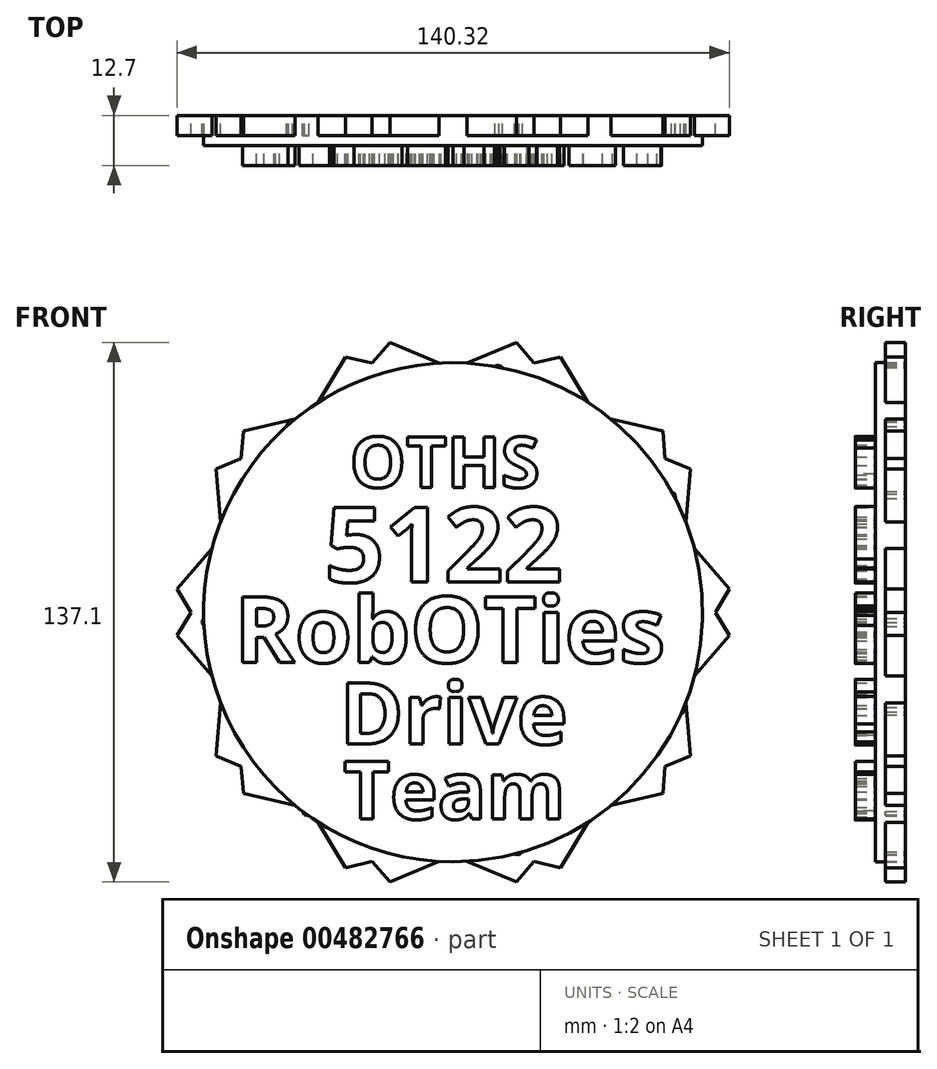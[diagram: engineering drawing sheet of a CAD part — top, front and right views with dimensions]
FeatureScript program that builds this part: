
annotation { "Feature Type Name" : "Feature", "Feature Type Description" : "" }
export const myFeature = defineFeature(function(context is Context, id is Id, definition is map)
    precondition{}
    {
        {
            var Q0;
            Q0=qCreatedBy(makeId("Front.planeOp"),FACE);
            var sketch = newSketch(context, id + "F0", { "sketchPlane" : qUnion([Q0])});
            skCircle(sketch, "E0.cCircle", {"center": v(0, 0) * mm, "radius": 63.4 * mm, "construction": true});
            skLineSegment(sketch, "E0.0", {"start": v(49.97, -39.02) * mm, "end": v(-8.8, -62.79) * mm});
            skLineSegment(sketch, "E0.1", {"start": v(-8.8, -62.79) * mm, "end": v(-58.78, -23.77) * mm});
            skLineSegment(sketch, "E0.2", {"start": v(-58.78, -23.77) * mm, "end": v(-49.97, 39.02) * mm});
            skLineSegment(sketch, "E0.3", {"start": v(-49.97, 39.02) * mm, "end": v(8.8, 62.79) * mm});
            skLineSegment(sketch, "E0.4", {"start": v(8.8, 62.79) * mm, "end": v(58.78, 23.77) * mm});
            skLineSegment(sketch, "E0.5", {"start": v(58.78, 23.77) * mm, "end": v(49.97, -39.02) * mm});
            skCircle(sketch, "E1", {"center": v(0, 0) * mm, "radius": 63.4 * mm});
            skSolve(sketch);
        }
        {
            var Q0;
            Q0=qSketchRegion(id+"F0",true);
            extrude(context, id + "F1", {"entities" : qUnion([Q0]), "depth" : 7.62 * mm});
        }
        {
            var Q0;
            Q0=qCreatedBy(makeId("Front.planeOp"),FACE);
            var sketch = newSketch(context, id + "F2", { "sketchPlane" : qUnion([Q0])});
            skCircle(sketch, "E2.cCircle", {"center": v(0, 0) * mm, "radius": 56.96 * mm, "construction": true});
            skLineSegment(sketch, "E2.0", {"start": v(70.16, -5.91) * mm, "end": v(16.06, -68.55) * mm});
            skLineSegment(sketch, "E2.1", {"start": v(16.06, -68.55) * mm, "end": v(-60.23, -36.45) * mm});
            skLineSegment(sketch, "E2.2", {"start": v(-60.23, -36.45) * mm, "end": v(-53.28, 46.02) * mm});
            skLineSegment(sketch, "E2.3", {"start": v(-53.28, 46.02) * mm, "end": v(27.3, 64.9) * mm});
            skLineSegment(sketch, "E2.4", {"start": v(27.3, 64.9) * mm, "end": v(70.16, -5.91) * mm});
            skPoint(sketch, "E2.0.midPoint", {"position": v(43.1, -37.23) * mm});
            skLineSegment(sketch, "E3.MirrorCS", {"start": v(-53.28, -46.02) * mm, "end": v(27.3, -64.9) * mm});
            skLineSegment(sketch, "E4.MirrorCS", {"start": v(27.3, -64.9) * mm, "end": v(70.16, 5.91) * mm});
            skLineSegment(sketch, "E5.MirrorCS", {"start": v(-60.23, 36.45) * mm, "end": v(-53.28, -46.02) * mm});
            skLineSegment(sketch, "E6.MirrorCS", {"start": v(70.16, 5.91) * mm, "end": v(16.06, 68.55) * mm});
            skLineSegment(sketch, "E7.MirrorCS", {"start": v(16.06, 68.55) * mm, "end": v(-60.23, 36.45) * mm});
            skLineSegment(sketch, "E8.MirrorCS", {"start": v(-27.3, 64.9) * mm, "end": v(-70.16, -5.91) * mm});
            skLineSegment(sketch, "E9.MirrorCS", {"start": v(-70.16, 5.91) * mm, "end": v(-16.06, 68.55) * mm});
            skLineSegment(sketch, "E10.MirrorCS", {"start": v(53.28, 46.02) * mm, "end": v(-27.3, 64.9) * mm});
            skLineSegment(sketch, "E11.MirrorCS", {"start": v(-16.06, 68.55) * mm, "end": v(60.23, 36.45) * mm});
            skLineSegment(sketch, "E12.MirrorCS", {"start": v(60.23, -36.45) * mm, "end": v(53.28, 46.02) * mm});
            skLineSegment(sketch, "E13.MirrorCS", {"start": v(60.23, 36.45) * mm, "end": v(53.28, -46.02) * mm});
            skLineSegment(sketch, "E14.MirrorCS", {"start": v(-16.06, -68.55) * mm, "end": v(60.23, -36.45) * mm});
            skLineSegment(sketch, "E15.MirrorCS", {"start": v(53.28, -46.02) * mm, "end": v(-27.3, -64.9) * mm});
            skLineSegment(sketch, "E16.MirrorCS", {"start": v(-70.16, -5.91) * mm, "end": v(-16.06, -68.55) * mm});
            skLineSegment(sketch, "E17.MirrorCS", {"start": v(-27.3, -64.9) * mm, "end": v(-70.16, 5.91) * mm});
            skCircle(sketch, "E18.cCircle", {"center": v(0, 0) * mm, "radius": 57.56 * mm, "construction": true});
            skLineSegment(sketch, "E18.0", {"start": v(58.64, -25.36) * mm, "end": v(16.73, -61.66) * mm});
            skLineSegment(sketch, "E18.1", {"start": v(16.73, -61.66) * mm, "end": v(-37.77, -51.52) * mm});
            skLineSegment(sketch, "E18.2", {"start": v(-37.77, -51.52) * mm, "end": v(-63.83, -2.6) * mm});
            skLineSegment(sketch, "E18.3", {"start": v(-63.83, -2.6) * mm, "end": v(-41.83, 48.3) * mm});
            skLineSegment(sketch, "E18.4", {"start": v(-41.83, 48.3) * mm, "end": v(11.68, 62.81) * mm});
            skLineSegment(sketch, "E18.5", {"start": v(11.68, 62.81) * mm, "end": v(56.39, 30.03) * mm});
            skLineSegment(sketch, "E18.6", {"start": v(56.39, 30.03) * mm, "end": v(58.64, -25.36) * mm});
            skPoint(sketch, "E18.0.midPoint", {"position": v(37.68, -43.5) * mm});
            skSolve(sketch);
        }
        {
            var Q0;
            Q0=qSketchRegion(id+"F2",true);
            extrude(context, id + "F3", {"entities" : qUnion([Q0]), "operationType" : NewBodyOperationType.ADD, "depth" : 5.08 * mm});
        }
        {
            var Q0;
            Q0=qCreatedBy(makeId("Front.planeOp"),FACE);
            var sketch = newSketch(context, id + "F4", { "sketchPlane" : qUnion([Q0])});
            skText(sketch, "E19", { "text": "OTHS", "fontName": "OpenSans-Bold.ttf"});
            skText(sketch, "E20", { "text": "5122", "fontName": "OpenSans-Bold.ttf"});
            skText(sketch, "E21", { "text": "RobOTies", "fontName": "OpenSans-Bold.ttf"});
            const initialGuessF4  = {"E19": [-0.02627, 0.03172, 1, 0, 0.01291], "E20": [-0.03266, 0.00766, 1, 0, 0.0191], "E21": [-0.05562, -0.0128, 1, 0, 0.01684]};
            skSetInitialGuess(sketch, initialGuessF4);
            skSolve(sketch);
        }
        {
            var Q0;
            Q0=qSketchRegion(id+"F4",true);
            extrude(context, id + "F5", {"entities" : qUnion([Q0]), "operationType" : NewBodyOperationType.ADD, "depth" : 5.08 * mm});
        }
        {
            var Q0;
            Q0=qSketchRegion(id+"F4",true);
            extrude(context, id + "F6", {"entities" : qUnion([Q0]), "operationType" : NewBodyOperationType.ADD, "depth" : 12.7 * mm});
        }
        {
            var Q0;
            Q0=qCreatedBy(makeId("Front.planeOp"),FACE);
            var sketch = newSketch(context, id + "F7", { "sketchPlane" : qUnion([Q0])});
            skText(sketch, "E22", { "text": "Drive", "fontName": "OpenSans-Bold.ttf"});
            skText(sketch, "E23", { "text": "Team", "fontName": "OpenSans-Bold.ttf"});
            const initialGuessF7  = {"E22": [-0.02873, -0.0335, 1, 0, 0.01564], "E23": [-0.02787, -0.05255, 1, 0, 0.01474]};
            skSetInitialGuess(sketch, initialGuessF7);
            skSolve(sketch);
        }
        {
            var Q0;
            Q0 = qSketchRegion(id + "F7", true);
            extrude(context, id + "F8", {"entities" : qUnion([Q0]), "operationType" : NewBodyOperationType.ADD, "depth" : 12.7 * mm});
        }
    });
